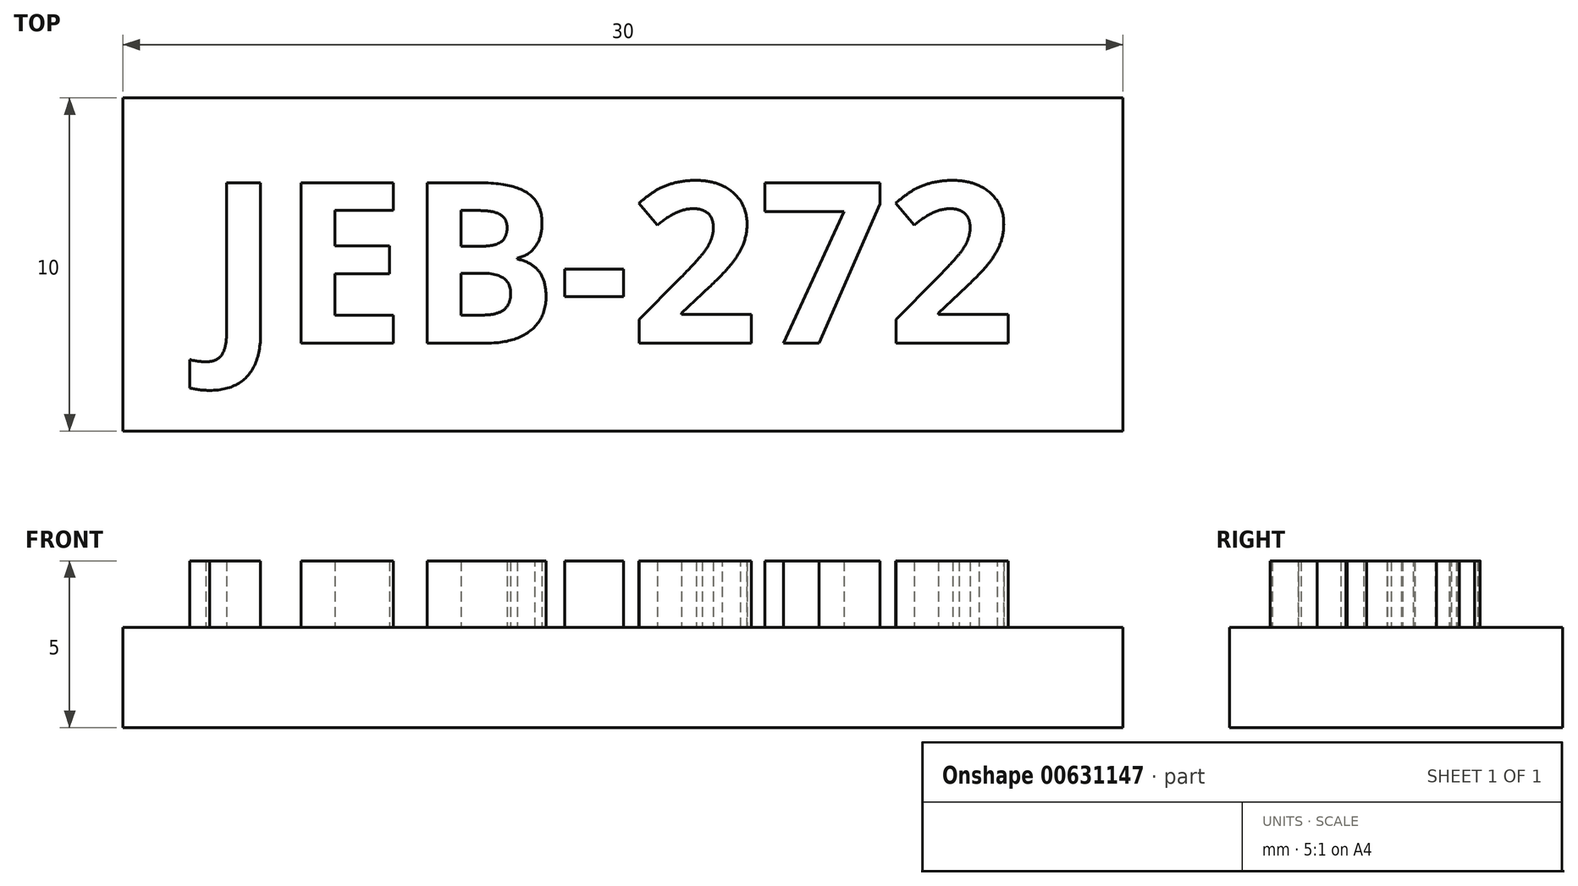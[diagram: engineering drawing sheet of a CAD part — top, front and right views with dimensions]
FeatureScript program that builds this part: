
annotation { "Feature Type Name" : "Feature", "Feature Type Description" : "" }
export const myFeature = defineFeature(function(context is Context, id is Id, definition is map)
    precondition{}
    {
        {
            var Q0;
            Q0=qCreatedBy(makeId("Top.planeOp"),FACE);
            var sketch = newSketch(context, id + "F0", { "sketchPlane" : qUnion([Q0])});
            skLineSegment(sketch, "E0.bottom", {"start": v(15, 5) * mm, "end": v(-15, 5) * mm});
            skLineSegment(sketch, "E0.top", {"start": v(15, -5) * mm, "end": v(-15, -5) * mm});
            skLineSegment(sketch, "E0.left", {"start": v(15, 5) * mm, "end": v(15, -5) * mm});
            skLineSegment(sketch, "E0.right", {"start": v(-15, 5) * mm, "end": v(-15, -5) * mm});
            skPoint(sketch, "E0.middle", {"position": v(0, 0) * mm});
            skSolve(sketch);
        }
        {
            var Q0;
            Q0=makeQuery(id+"F0.imprint","IMPRINT",FACE,{"disambiguationData":[TD([[makeQuery(id+"F0.imprint","IMPRINT",EDGE,{"derivedFrom":sQuery(id+"F0.wireOp",EDGE,"E0.bottom")}),1.0]])]});
            extrude(context, id + "F1", {"entities" : qUnion([Q0]), "depth" : 3 * mm, "offsetDistance" : 25.4 * mm});
        }
        {
            var Q0;
            Q0=makeQuery(id+"F1.opExtrude","CAP_FACE",FACE,{"disambiguationData":[OSD([sQuery(id+"F0.wireOp",EDGE,"E0.bottom"),sQuery(id+"F0.wireOp",EDGE,"E0.top"),sQuery(id+"F0.wireOp",EDGE,"E0.left"),sQuery(id+"F0.wireOp",EDGE,"E0.right")])],"isStart":false});
            var sketch = newSketch(context, id + "F2", { "sketchPlane" : qUnion([Q0])});
            skText(sketch, "E1", { "text": "JEB-272", "fontName": "OpenSans-Bold.ttf"});
            const initialGuessF2  = {"E1": [-0.0125, -0.00236, 1, 0, 0.00486]};
            skSetInitialGuess(sketch, initialGuessF2);
            skSolve(sketch);
        }
        {
            var Q0;
            Q0=makeQuery(id+"F2.imprint","IMPRINT",FACE,{"disambiguationData":[TD([[makeQuery(id+"F2.imprint","IMPRINT",EDGE,{"derivedFrom":sQuery(id+"F2.wireOp",EDGE,"E1.sketch_text.stroke-22")}),-1.0]])]});
            var Q1;
            Q1=makeQuery(id+"F2.imprint","IMPRINT",FACE,{"disambiguationData":[TD([[makeQuery(id+"F2.imprint","IMPRINT",EDGE,{"derivedFrom":sQuery(id+"F2.wireOp",EDGE,"E1.sketch_text.stroke-10")}),-1.0]])]});
            var Q2;
            Q2=makeQuery(id+"F2.imprint","IMPRINT",FACE,{"disambiguationData":[TD([[makeQuery(id+"F2.imprint","IMPRINT",EDGE,{"derivedFrom":sQuery(id+"F2.wireOp",EDGE,"E1.sketch_text.stroke-75")}),-1.0]])]});
            var Q3;
            Q3=makeQuery(id+"F2.imprint","IMPRINT",FACE,{"disambiguationData":[TD([[makeQuery(id+"F2.imprint","IMPRINT",EDGE,{"derivedFrom":sQuery(id+"F2.wireOp",EDGE,"E1.sketch_text.stroke-47")}),-1.0]])]});
            var Q4;
            Q4=makeQuery(id+"F2.imprint","IMPRINT",FACE,{"disambiguationData":[TD([[makeQuery(id+"F2.imprint","IMPRINT",EDGE,{"derivedFrom":sQuery(id+"F2.wireOp",EDGE,"E1.sketch_text.stroke-82")}),-1.0]])]});
            var Q5;
            Q5=makeQuery(id+"F2.imprint","IMPRINT",FACE,{"disambiguationData":[TD([[makeQuery(id+"F2.imprint","IMPRINT",EDGE,{"derivedFrom":sQuery(id+"F2.wireOp",EDGE,"E1.sketch_text.stroke-0")}),-1.0]])]});
            var Q6;
            Q6=makeQuery(id+"F2.imprint","IMPRINT",FACE,{"disambiguationData":[TD([[makeQuery(id+"F2.imprint","IMPRINT",EDGE,{"derivedFrom":sQuery(id+"F2.wireOp",EDGE,"E1.sketch_text.stroke-51")}),-1.0]])]});
            extrude(context, id + "F3", {"entities" : qUnion([Q0, Q1, Q2, Q3, Q4, Q5, Q6]), "operationType" : NewBodyOperationType.ADD, "depth" : 2 * mm, "offsetDistance" : 25.4 * mm});
        }
    });
